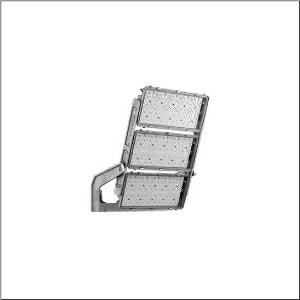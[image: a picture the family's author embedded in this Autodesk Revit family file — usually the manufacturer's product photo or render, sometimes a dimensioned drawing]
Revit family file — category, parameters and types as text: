
# Revit family: floodlight_fl_11_maxi_pro_remote___pl64blc_5xa779424w01aa_0c8b
name_source: partatom
category: Lighting Fixtures
units: mm (PartAtom-declared; Revit-internal decimal feet)

## family parameters
Cut with Voids When Loaded = No
Host = Face
Light Source = No
Part Type = Normal
Room Calculation Point = No
Round Connector Dimension = Use Diameter
Shared = No

## types (1)
- --- (1 x LED, 110040 lm, 1516.7 W, 5700K)
    Apparent Load = 1517 VA
    CIE Flux Codes = 28 83 99 100 100
    Color Rendering = 90
    Color Temperature = 5700K
    Default Elevation = 1800 mm
    Description = Floodlight FL 11  maxi  pro Remote floodlight; light control with lens of PMMA; cover panel of toughened safety glass, transparent; light distribution: PL64BLC, asymmetric direct distribution, LEDcolour temperature: 5700K, rated luminous flux: 110.040lm, colour rendering: CRI > 90, light colour: 957; luminous efficacy: 73lm/W; brightness control: DALI 2 (1 DALI address); with terminal, 8-pole, max. 2.5mm², mains connection: 220..240V/380..400V AC, 50/60Hz, surge voltage resistance: line to ground: 10kV, ECG replaceable separately, no afterglow with DALI off / DMX off command, LED unit replaceable without ESD environment, dustproof LED module, dimming range 10..100%; 1517W floodlight with 3x LED unit of diecast aluminium, coated grey; length: 1.003mm / width: 651mm / height: 338mm; mounting bracket, of diecast aluminium, uncoated, natural, equipment: Power, protection rating (complete): IP66; insulation class (complete): insulation class I (protective earthing); certification: CE; ball protection: ball impact resistance with accessories, impact resistance: IK07; only for outdoor installations, rated ambient temperature 10°C, permissible operating ambient temperature: -40..+30°C, permissible storage temperature: -40..+85°Cpackaging unit: 1 piece

Light Distribution: PL64BLC
    Height = 320 mm
    Lamp = 1 x LED
    Lamp Light Flux = 110040 lm
    Lamp Power = 1516.7 W
    Lamp count = 1
    Length = 1002 mm
    Luminous efficacy = 73 lm/W
    Manufacturer = Siteco
    ModVariant = No
    Model = 5XA779424W01AA
    Mounting Place = Ceiling
    Mounting Type = Surface mounted
    Number of Poles = 1
    OnlyDefault = Yes
    Power Factor = 1
    Product Name = Floodlight FL 11 maxi pro Remote | PL64BLC
    Product group = floodlight | ceiling mounted
    ProductGroupID = 301
    Protection Class = Protection class I
    Protection Degree = IP 66
    RLX_Detail_Level = 1
    RLX_Emergency_Light_Flux = 0 lm
    RLX_Emergency_Type = 0
    RLX_Emergency_Type_DB = No
    RlxData = <blob elided: 52309 chars, md5=7d338dfa>
    Socket = socket
    Standby Power = 0 W
    System Light Flux = 110040 lm
    System Power = 1517 W
    Type Comments = factory setting: luminous flux: 100 % | dim-lin: 254 | 1070 mA
    Type Image = l_1349141.jpg
    URL = http://relux.com
    VarID = @adj_080316
    Voltage = 0 V
    Weight = 0.00 kg
    Width = 655 mm

## geometry (parser evidence)
native form markers: Blend x4, Sweep x13
no freeform markers — native parametric forms only
